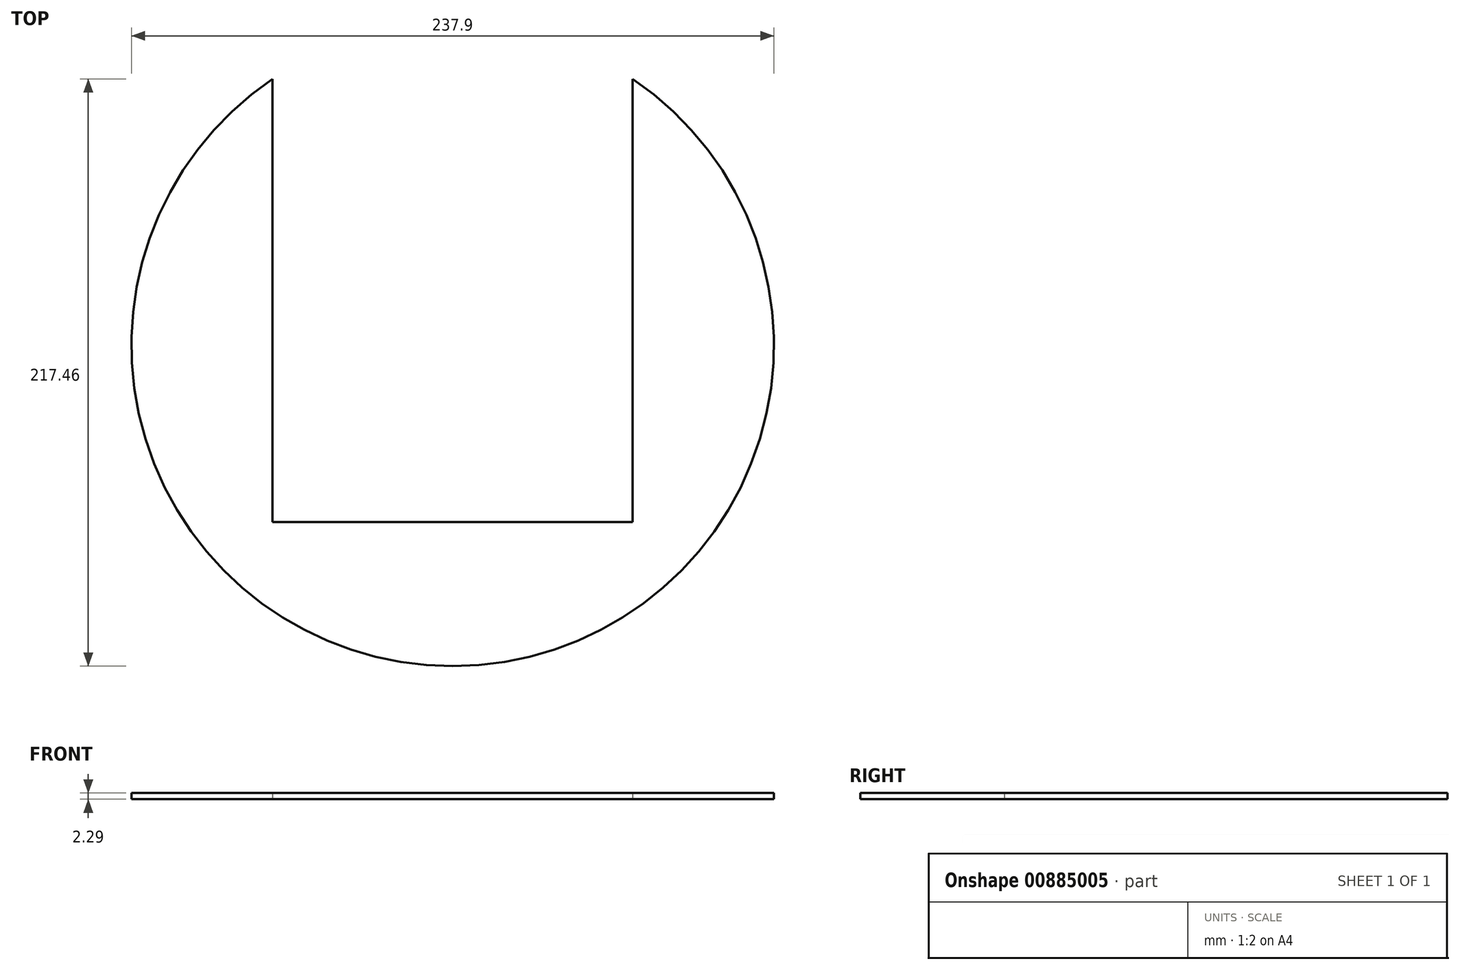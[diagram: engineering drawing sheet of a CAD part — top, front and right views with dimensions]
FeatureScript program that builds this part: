
annotation { "Feature Type Name" : "Feature", "Feature Type Description" : "" }
export const myFeature = defineFeature(function(context is Context, id is Id, definition is map)
    precondition{}
    {
        {
            var Q0;
            Q0=qCreatedBy(makeId("Top.planeOp"),FACE);
            var sketch = newSketch(context, id + "F0", { "sketchPlane" : qUnion([Q0])});
            skLineSegment(sketch, "E0.bottom", {"start": v(-47.06, 107.68) * mm, "end": v(86.3, 107.68) * mm});
            skLineSegment(sketch, "E0.top", {"start": v(-47.06, -56.45) * mm, "end": v(86.3, -56.45) * mm});
            skLineSegment(sketch, "E0.left", {"start": v(-47.06, 107.68) * mm, "end": v(-47.06, -56.45) * mm});
            skLineSegment(sketch, "E0.right", {"start": v(86.3, 107.68) * mm, "end": v(86.3, -56.45) * mm});
            skArc(sketch, "E1", {"start": v(-47.06, 107.68) * mm, "mid": v(19.62, -109.78) * mm, "end": v(86.3, 107.68) * mm});
            skSolve(sketch);
        }
        {
            var Q0;
            Q0=makeQuery(id+"F0.imprint","IMPRINT",FACE,{"disambiguationData":[TD([[makeQuery(id+"F0.imprint","IMPRINT",EDGE,{"derivedFrom":sQuery(id+"F0.wireOp",EDGE,"E0.top")}),-1.0]])]});
            extrude(context, id + "F1", {"entities" : qUnion([Q0]), "depth" : 2.3 * mm, "offsetDistance" : 25.4 * mm});
        }
    });
